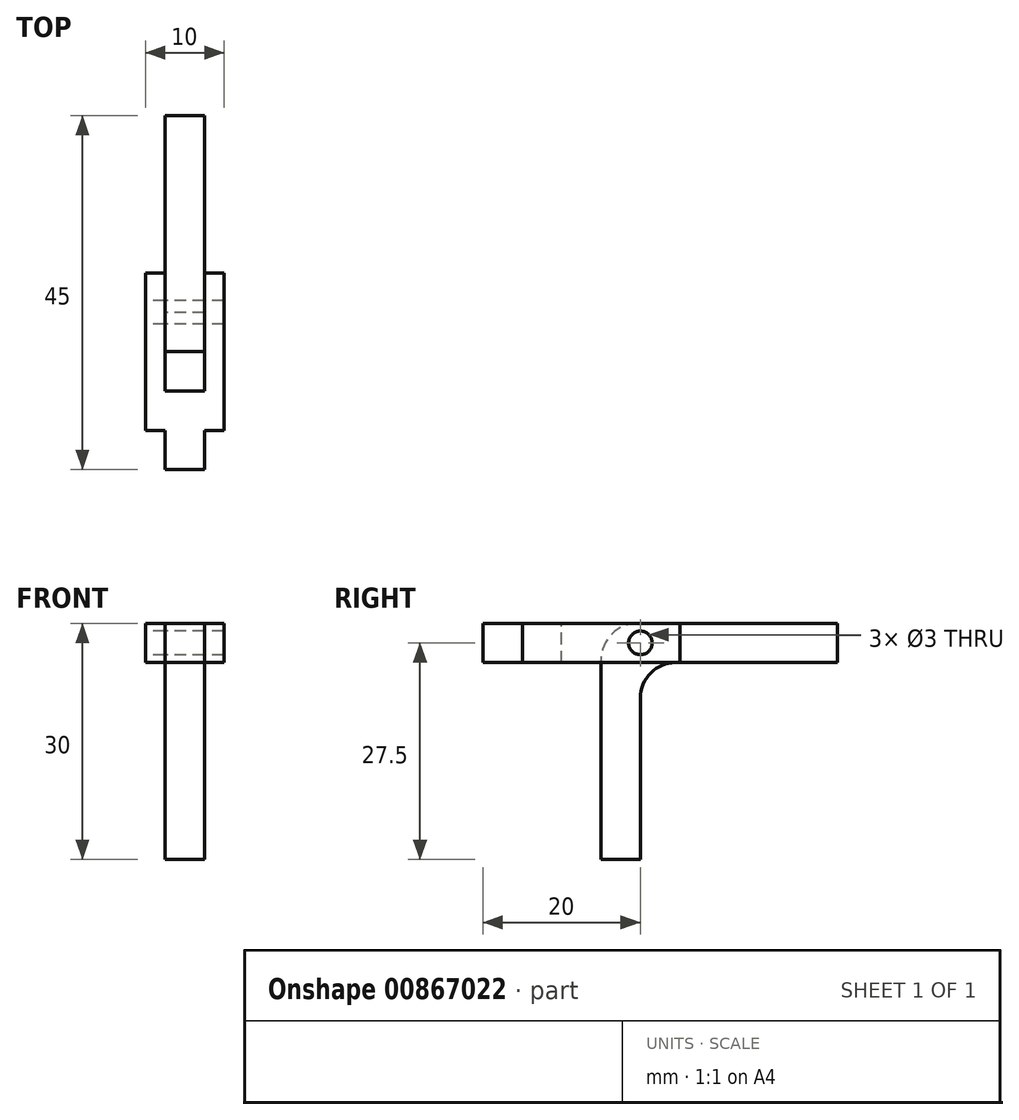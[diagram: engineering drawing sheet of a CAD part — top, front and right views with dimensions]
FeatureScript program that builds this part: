
annotation { "Feature Type Name" : "Feature", "Feature Type Description" : "" }
export const myFeature = defineFeature(function(context is Context, id is Id, definition is map)
    precondition{}
    {
        {
            var Q0;
            Q0=qCreatedBy(makeId("Right.planeOp"),FACE);
            var sketch = newSketch(context, id + "F0", { "sketchPlane" : qUnion([Q0])});
            skLineSegment(sketch, "E0", {"start": v(4.7, 0) * mm, "end": v(30, 0) * mm});
            skLineSegment(sketch, "E1", {"start": v(30, 0) * mm, "end": v(30, -5) * mm});
            skLineSegment(sketch, "E2", {"start": v(0, -5) * mm, "end": v(0, -4.7) * mm});
            skLineSegment(sketch, "E3", {"start": v(0, -5) * mm, "end": v(0, -30) * mm});
            skLineSegment(sketch, "E4", {"start": v(0, -30) * mm, "end": v(5, -30) * mm});
            skLineSegment(sketch, "E5", {"start": v(5, -30) * mm, "end": v(5, -9.5) * mm});
            skLineSegment(sketch, "E6", {"start": v(5, -5) * mm, "end": v(0, -5) * mm, "construction": true});
            skLineSegment(sketch, "E7", {"start": v(2.5, -5) * mm, "end": v(2.5, 0) * mm, "construction": true});
            skLineSegment(sketch, "E8", {"start": v(9.5, -5) * mm, "end": v(30, -5) * mm});
            skPoint(sketch, "E9.visualSharp", {"position": v(0, 0) * mm});
            skArc(sketch, "E9.filletArc", {"start": v(4.7, 0) * mm, "mid": v(1.38, -1.38) * mm, "end": v(0, -4.7) * mm});
            skPoint(sketch, "E10.visualSharp", {"position": v(5, -5) * mm});
            skArc(sketch, "E10.filletArc", {"start": v(9.5, -5) * mm, "mid": v(6.32, -6.32) * mm, "end": v(5, -9.5) * mm});
            skCircle(sketch, "E11", {"center": v(20, -20) * mm, "radius": 15 * mm, "construction": true});
            skSolve(sketch);
        }
        {
            var Q0;
            Q0 = qSketchRegion(id + "F0", true);
            extrude(context, id + "F1", {"entities" : qUnion([Q0]), "depth" : 5 * mm, "offsetDistance" : 25 * mm});
        }
        {
            var Q0;
            Q0=makeQuery(id+"F1.opExtrude","SWEPT_FACE",FACE,{"disambiguationData":[OSD([sQuery(id+"F0.wireOp",EDGE,"E0")])]});
            var sketch = newSketch(context, id + "F2", { "sketchPlane" : qUnion([Q0])});
            skLineSegment(sketch, "E12", {"start": v(5, 10) * mm, "end": v(7.5, 10) * mm});
            skLineSegment(sketch, "E13", {"start": v(7.5, 10) * mm, "end": v(7.5, -10) * mm});
            skLineSegment(sketch, "E14", {"start": v(7.5, -10) * mm, "end": v(5, -10) * mm});
            skLineSegment(sketch, "E15", {"start": v(-2.5, -10) * mm, "end": v(-2.5, 10) * mm});
            skLineSegment(sketch, "E16", {"start": v(-2.5, 10) * mm, "end": v(0, 10) * mm});
            skLineSegment(sketch, "E17", {"start": v(0, 10) * mm, "end": v(0, -5) * mm});
            skLineSegment(sketch, "E18", {"start": v(0, -5) * mm, "end": v(5, -5) * mm});
            skLineSegment(sketch, "E19", {"start": v(5, -5) * mm, "end": v(5, 10) * mm});
            skLineSegment(sketch, "E20", {"start": v(2.5, -5) * mm, "end": v(2.5, -10) * mm, "construction": true});
            skLineSegment(sketch, "E21", {"start": v(0, -10) * mm, "end": v(0, -15) * mm});
            skLineSegment(sketch, "E22", {"start": v(5, -10) * mm, "end": v(5, -15) * mm});
            skLineSegment(sketch, "E23.trimOffspring", {"start": v(0, -10) * mm, "end": v(-2.5, -10) * mm});
            skLineSegment(sketch, "E24", {"start": v(0, -15) * mm, "end": v(5, -15) * mm});
            skSolve(sketch);
        }
        {
            var Q0;
            Q0 = qSketchRegion(id + "F2", true);
            var Q1;
            Q1=makeQuery(id+"F1.opExtrude","SWEPT_FACE",FACE,{"disambiguationData":[OSD([sQuery(id+"F0.wireOp",EDGE,"E8")])]});
            extrude(context, id + "F3", {"entities" : qUnion([Q0]), "endBound" : BoundingType.UP_TO_SURFACE, "oppositeDirection" : true, "depth" : 25 * mm, "endBoundEntityFace" : qUnion([Q1]), "offsetDistance" : 25 * mm});
        }
        {
            var Q0;
            Q0=makeQuery(id+"F3.opExtrude","SWEPT_FACE",FACE,{"disambiguationData":[OSD([sQuery(id+"F2.wireOp",EDGE,"E15")])]});
            var sketch = newSketch(context, id + "F4", { "sketchPlane" : qUnion([Q0])});
            skCircle(sketch, "E25", {"center": v(-5, -2.5) * mm, "radius": 1.5 * mm});
            skSolve(sketch);
        }
        {
            var Q0;
            Q0 = qSketchRegion(id + "F4", true);
            var Q1;
            Q1=makeQuery(id+"F3.opExtrude","SWEPT_FACE",FACE,{"disambiguationData":[OSD([sQuery(id+"F2.wireOp",EDGE,"E13")])]});
            extrude(context, id + "F5", {"entities" : qUnion([Q0]), "operationType" : NewBodyOperationType.REMOVE, "endBound" : BoundingType.UP_TO_SURFACE, "oppositeDirection" : true, "depth" : 25 * mm, "endBoundEntityFace" : qUnion([Q1]), "offsetDistance" : 25 * mm});
        }
    });
